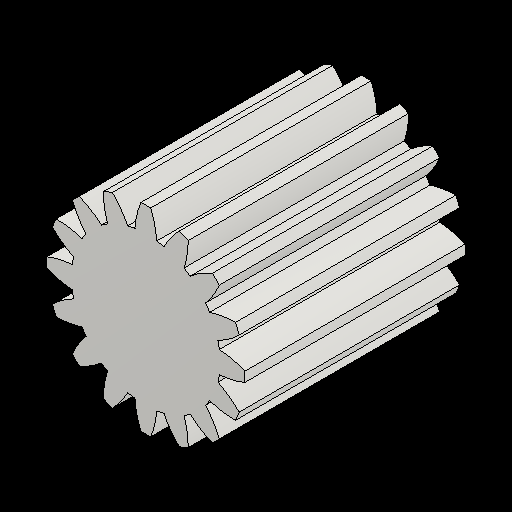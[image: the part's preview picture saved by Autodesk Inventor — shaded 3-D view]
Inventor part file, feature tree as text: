
AUTODESK INVENTOR PART (.ipt)
format: ipt  version: 2023.2 (Build 272271030, 271C)  size: 202,752 bytes
history: native  units: mm (DEFAULTED — no unit token found)
features: plane x3, other x3, sketch x2, extrude x1
ambient origin geometry x8: Origin, YZ Plane, XZ Plane, XY Plane, X Axis, Y Axis, Z Axis, Center Point
bodies: Solid1 (feature_tree)
feature tree (9):
  extrude  "Extrusion1"  Depth=20.0mm TaperAngle=0.0deg
  plane  "Work Plane2"
  plane  "Work Plane8"
  plane  "Work Plane9"
  other  "Spur Gear"
  sketch  "Sketch1"  dims[d0=18.0mm d1=20.0mm d2=0.0mm]
  sketch  "Sketch2"  dims[d3=16.0mm d4=10.0mm d5=0.0mm d16=12.0mm d17=0.0mm d34=1.963495mm d39=0.0mm d41=0.0mm d43=12.0mm d46=12.0mm d47=0.0mm d48=0.0mm]
  other  "Srf1"
  other  "Pitch Diameter"
